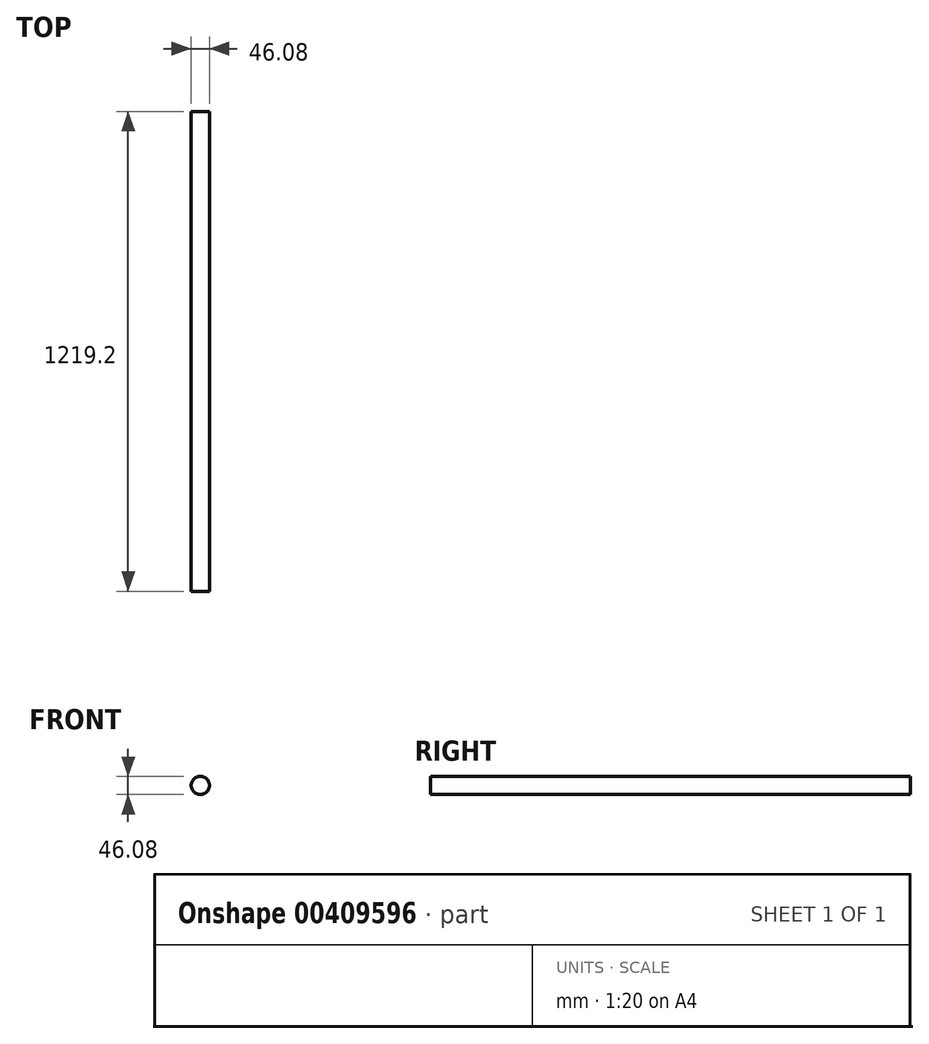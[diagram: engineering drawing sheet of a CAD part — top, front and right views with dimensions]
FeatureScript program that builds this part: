
annotation { "Feature Type Name" : "Feature", "Feature Type Description" : "" }
export const myFeature = defineFeature(function(context is Context, id is Id, definition is map)
    precondition{}
    {
        {
            var Q0;
            Q0=qCreatedBy(makeId("Front.planeOp"),FACE);
            var sketch = newSketch(context, id + "F0", { "sketchPlane" : qUnion([Q0])});
            skCircle(sketch, "E0", {"center": v(0, 0) * mm, "radius": 23.04 * mm});
            skSolve(sketch);
        }
        {
            var Q0;
            Q0=sQuery(id+"F0.wireOp",EDGE,"E0");
            extrude(context, id + "F1", {"bodyType" : ToolBodyType.SURFACE, "surfaceEntities" : qUnion([Q0]), "depth" : 1219.2 * mm});
        }
    });
